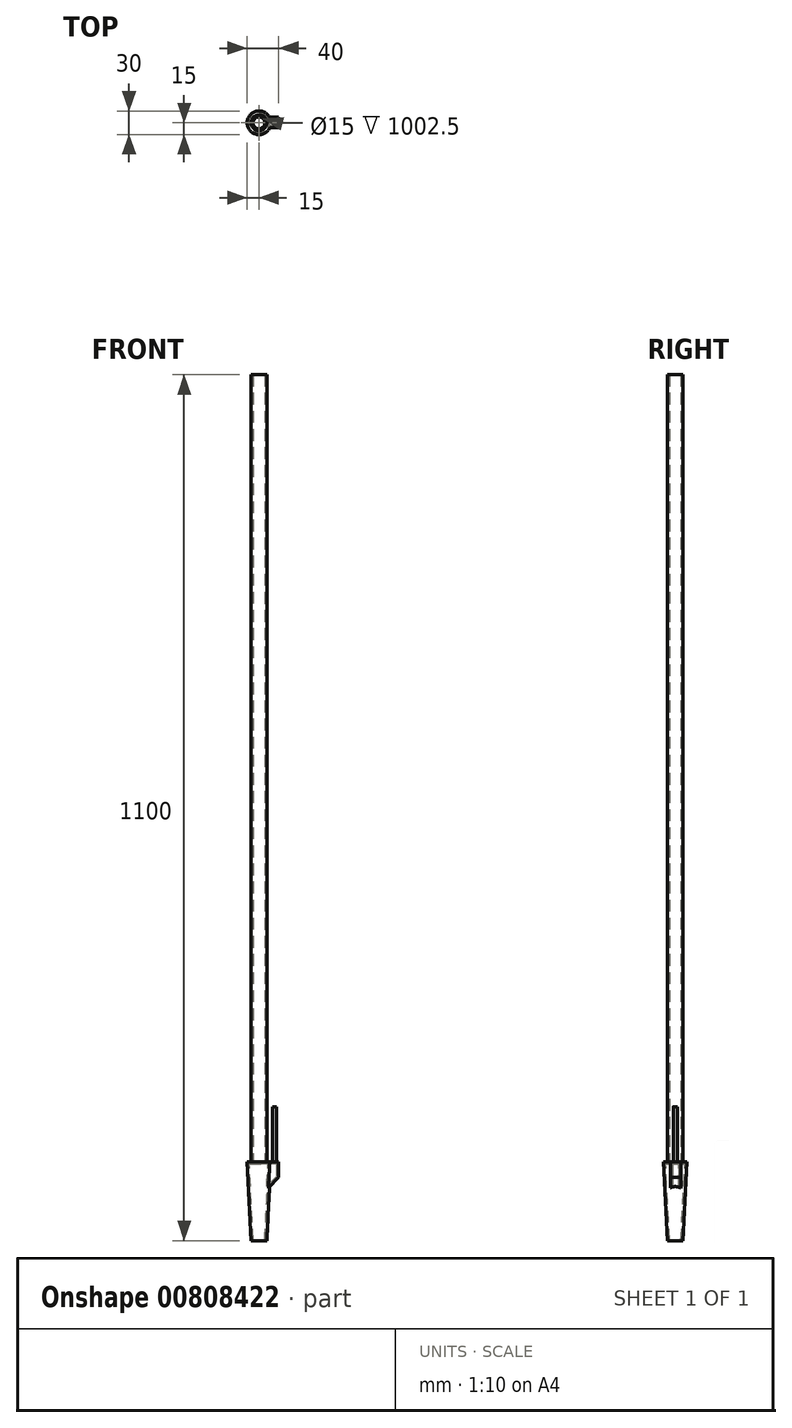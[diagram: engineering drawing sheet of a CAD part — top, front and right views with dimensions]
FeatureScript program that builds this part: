
annotation { "Feature Type Name" : "Feature", "Feature Type Description" : "" }
export const myFeature = defineFeature(function(context is Context, id is Id, definition is map)
    precondition{}
    {
        {
            var Q0;
            Q0=qCreatedBy(makeId("Top.planeOp"),FACE);
            var sketch = newSketch(context, id + "F0", { "sketchPlane" : qUnion([Q0])});
            skCircle(sketch, "E0", {"center": v(0, 0) * mm, "radius": 10 * mm});
            skSolve(sketch);
        }
        {
            var Q0;
            Q0=qCreatedBy(makeId("Top.planeOp"),FACE);
            cPlane(context, id + "F1", {"entities" : qUnion([Q0]), "cplaneType" : CPlaneType.OFFSET, "offset" : 100 * mm, "width" : 150 * mm, "height" : 150 * mm});
        }
        {
            var Q0;
            Q0=qCreatedBy(id+"F1.planeOp",FACE);
            var sketch = newSketch(context, id + "F2", { "sketchPlane" : qUnion([Q0])});
            skCircle(sketch, "E1", {"center": v(0, 0) * mm, "radius": 15 * mm});
            skSolve(sketch);
        }
        {
            var Q0;
            Q0=makeQuery(id+"F0.imprint","IMPRINT",FACE,{"disambiguationData":[TD([[makeQuery(id+"F0.imprint","IMPRINT",EDGE,{"derivedFrom":sQuery(id+"F0.wireOp",EDGE,"E0")}),1.0]])]});
            var Q1;
            Q1=makeQuery(id+"F2.imprint","IMPRINT",FACE,{"disambiguationData":[TD([[makeQuery(id+"F2.imprint","IMPRINT",EDGE,{"derivedFrom":sQuery(id+"F2.wireOp",EDGE,"E1")}),1.0]])]});
            loft(context, id + "F3", {"sheetProfilesArray" : [{ "sheetProfileEntities" : qUnion([Q0]) }, { "sheetProfileEntities" : qUnion([Q1]) }]});
        }
        {
            var Q0;
            Q0=makeQuery(id+"F3.opLoft","CAP_FACE",FACE,{"disambiguationData":[OSD([makeQuery(id+"F2.imprint","IMPRINT",FACE,{"disambiguationData":[TD([[makeQuery(id+"F2.imprint","IMPRINT",EDGE,{"derivedFrom":sQuery(id+"F2.wireOp",EDGE,"E1")}),1.0]])]})])],"isStart":true});
            var sketch = newSketch(context, id + "F4", { "sketchPlane" : qUnion([Q0])});
            skCircle(sketch, "E2", {"center": v(0, 0) * mm, "radius": 10 * mm});
            skSolve(sketch);
        }
        {
            var Q0;
            Q0=makeQuery(id+"F4.imprint","IMPRINT",FACE,{"disambiguationData":[TD([[makeQuery(id+"F4.imprint","IMPRINT",EDGE,{"derivedFrom":sQuery(id+"F4.wireOp",EDGE,"E2")}),1.0]])]});
            extrude(context, id + "F5", {"entities" : qUnion([Q0]), "operationType" : NewBodyOperationType.ADD, "depth" : 1000 * mm, "offsetDistance" : 25 * mm});
        }
        {
            var Q0;
            Q0=qCreatedBy(makeId("Right.planeOp"),FACE);
            var sketch = newSketch(context, id + "F6", { "sketchPlane" : qUnion([Q0])});
            skLineSegment(sketch, "E3", {"start": v(-48.4, 100) * mm, "end": v(42.02, 100) * mm, "construction": true});
            skLineSegment(sketch, "E4.bottom", {"start": v(6.98, 100) * mm, "end": v(-5.89, 100) * mm});
            skLineSegment(sketch, "E4.top", {"start": v(6.98, 65.2) * mm, "end": v(-5.89, 65.2) * mm});
            skLineSegment(sketch, "E4.left", {"start": v(6.98, 100) * mm, "end": v(6.98, 65.2) * mm});
            skLineSegment(sketch, "E4.right", {"start": v(-5.89, 100) * mm, "end": v(-5.89, 65.2) * mm});
            skSolve(sketch);
        }
        {
            var Q0;
            Q0 = qSketchRegion(id + "F6", true);
            extrude(context, id + "F7", {"entities" : qUnion([Q0]), "operationType" : NewBodyOperationType.ADD, "depth" : 25 * mm, "offsetDistance" : 25 * mm});
        }
        {
            var Q0;
            Q0=makeQuery(id+"F7.boolean.opBoolean","MERGE",FACE,{"derivedFrom":[makeQuery(id+"F3.opLoft","CAP_FACE",FACE,{"disambiguationData":[OSD([makeQuery(id+"F2.imprint","IMPRINT",FACE,{"disambiguationData":[TD([[makeQuery(id+"F2.imprint","IMPRINT",EDGE,{"derivedFrom":sQuery(id+"F2.wireOp",EDGE,"E1")}),1.0]])]})])],"isStart":true}),makeQuery(id+"F7.opExtrude","SWEPT_FACE",FACE,{"disambiguationData":[OSD([sQuery(id+"F6.wireOp",EDGE,"E4.bottom")])]})]});
            var sketch = newSketch(context, id + "F8", { "sketchPlane" : qUnion([Q0])});
            skCircle(sketch, "E5", {"center": v(20, 0) * mm, "radius": 2.5 * mm});
            skSolve(sketch);
        }
        {
            var Q0;
            Q0 = qSketchRegion(id + "F8", true);
            extrude(context, id + "F9", {"entities" : qUnion([Q0]), "operationType" : NewBodyOperationType.ADD, "depth" : 70 * mm, "offsetDistance" : 25 * mm});
        }
        {
            var Q0;
            Q0=makeQuery(id+"F7.opExtrude","CAP_EDGE",EDGE,{"disambiguationData":[OSD([sQuery(id+"F6.wireOp",EDGE,"E4.top")])],"isStart":false});
            chamfer(context, id + "F10", {"entities" : qUnion([Q0]), "width" : 15 * mm, "tangentPropagation" : true});
        }
        {
            var Q0;
            Q0=makeQuery(id+"F3.opLoft","CAP_FACE",FACE,{"disambiguationData":[OSD([makeQuery(id+"F0.imprint","IMPRINT",FACE,{"disambiguationData":[TD([[makeQuery(id+"F0.imprint","IMPRINT",EDGE,{"derivedFrom":sQuery(id+"F0.wireOp",EDGE,"E0")}),1.0]])]})])],"isStart":true});
            var Q1;
            Q1=makeQuery(id+"F5.opExtrude","CAP_FACE",FACE,{"disambiguationData":[OSD([sQuery(id+"F4.wireOp",EDGE,"E2")])],"isStart":false});
            shell(context, id + "F11", {"entities" : qUnion([Q0, Q1]), "thickness" : 2.5 * mm});
        }
    });
